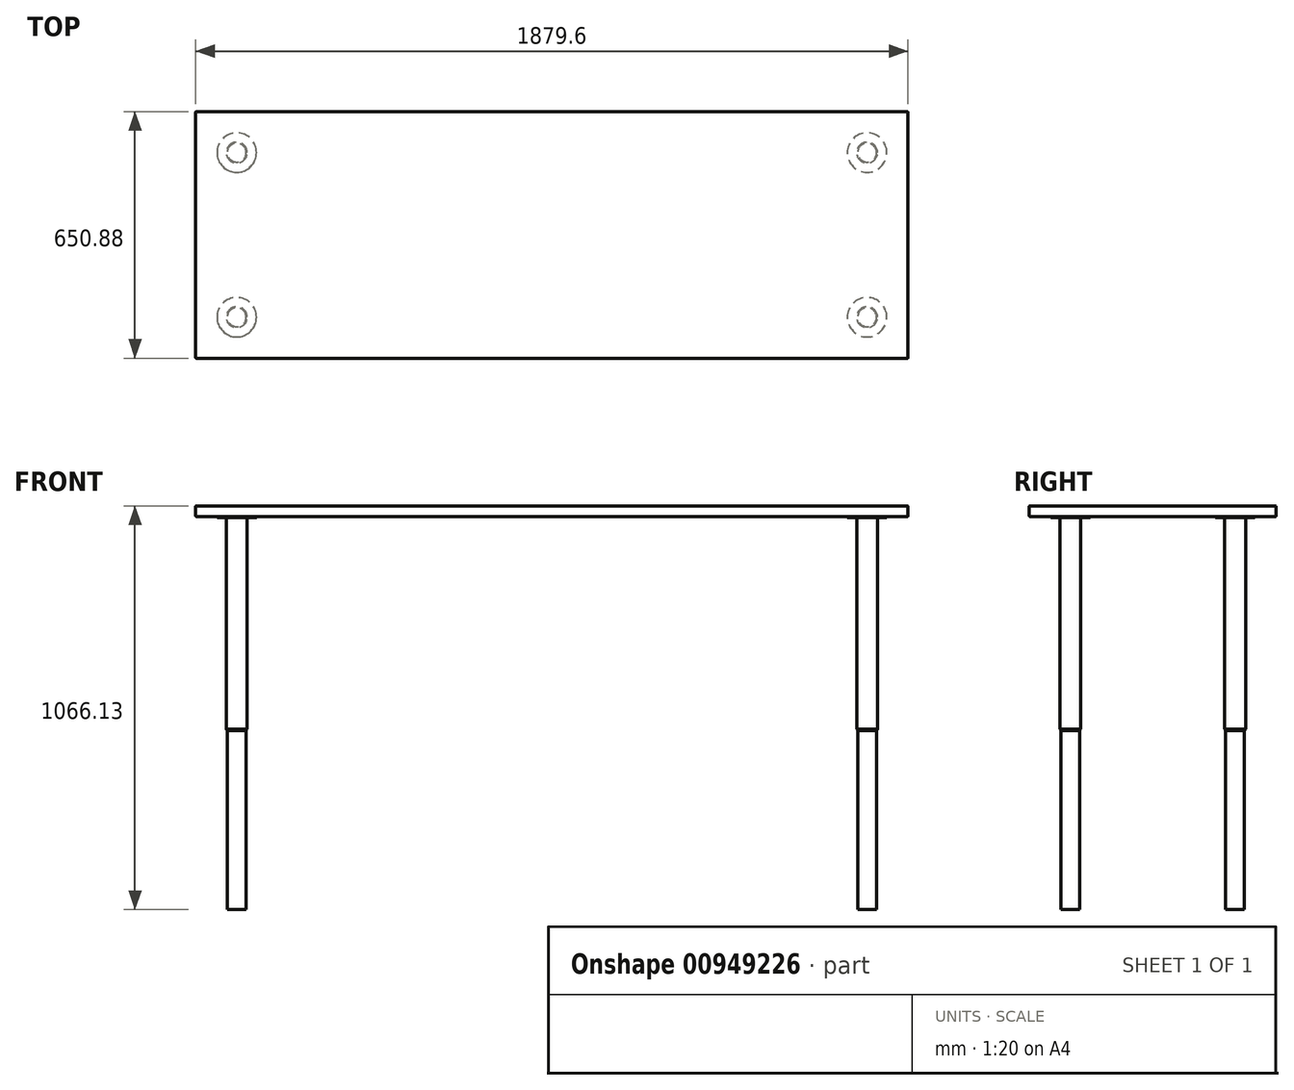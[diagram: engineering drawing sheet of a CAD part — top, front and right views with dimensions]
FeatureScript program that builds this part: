
annotation { "Feature Type Name" : "Feature", "Feature Type Description" : "" }
export const myFeature = defineFeature(function(context is Context, id is Id, definition is map)
    precondition{}
    {
        {
            var Q0;
            Q0=qCreatedBy(makeId("Top.planeOp"),FACE);
            var sketch = newSketch(context, id + "F0", { "sketchPlane" : qUnion([Q0])});
            skLineSegment(sketch, "E0.bottom", {"start": v(-939.8, 325.44) * mm, "end": v(939.8, 325.44) * mm});
            skLineSegment(sketch, "E0.top", {"start": v(-939.8, -325.44) * mm, "end": v(939.8, -325.44) * mm});
            skLineSegment(sketch, "E0.left", {"start": v(-939.8, 325.44) * mm, "end": v(-939.8, -325.44) * mm});
            skLineSegment(sketch, "E0.right", {"start": v(939.8, 325.44) * mm, "end": v(939.8, -325.44) * mm});
            skPoint(sketch, "E0.middle", {"position": v(0, 0) * mm});
            skSolve(sketch);
        }
        {
            var Q0;
            Q0 = qSketchRegion(id + "F0", true);
            extrude(context, id + "F1", {"entities" : qUnion([Q0]), "depth" : 28.2 * mm, "offsetDistance" : 25 * mm});
        }
        {
            var Q0;
            Q0=makeQuery(id+"F1.opExtrude","CAP_EDGE",EDGE,{"disambiguationData":[OSD([sQuery(id+"F0.wireOp",EDGE,"E0.top")])],"isStart":false});
            var Q1;
            Q1=makeQuery(id+"F1.opExtrude","CAP_EDGE",EDGE,{"disambiguationData":[OSD([sQuery(id+"F0.wireOp",EDGE,"E0.top")])],"isStart":true});
            var Q2;
            Q2=makeQuery(id+"F1.opExtrude","CAP_EDGE",EDGE,{"disambiguationData":[OSD([sQuery(id+"F0.wireOp",EDGE,"E0.left")])],"isStart":false});
            var Q3;
            Q3=makeQuery(id+"F1.opExtrude","CAP_EDGE",EDGE,{"disambiguationData":[OSD([sQuery(id+"F0.wireOp",EDGE,"E0.bottom")])],"isStart":false});
            var Q4;
            Q4=makeQuery(id+"F1.opExtrude","CAP_EDGE",EDGE,{"disambiguationData":[OSD([sQuery(id+"F0.wireOp",EDGE,"E0.right")])],"isStart":false});
            var Q5;
            Q5=makeQuery(id+"F1.opExtrude","CAP_EDGE",EDGE,{"disambiguationData":[OSD([sQuery(id+"F0.wireOp",EDGE,"E0.right")])],"isStart":true});
            var Q6;
            Q6=makeQuery(id+"F1.opExtrude","CAP_EDGE",EDGE,{"disambiguationData":[OSD([sQuery(id+"F0.wireOp",EDGE,"E0.bottom")])],"isStart":true});
            var Q7;
            Q7=makeQuery(id+"F1.opExtrude","CAP_EDGE",EDGE,{"disambiguationData":[OSD([sQuery(id+"F0.wireOp",EDGE,"E0.left")])],"isStart":true});
            var Q8;
            Q8=makeQuery(id+"F1.opExtrude","SWEPT_EDGE",EDGE,{"disambiguationData":[OSD([sQuery(id+"F0.wireOp",EDGE,"E0.top"),sQuery(id+"F0.wireOp",EDGE,"E0.left")])]});
            var Q9;
            Q9=makeQuery(id+"F1.opExtrude","SWEPT_EDGE",EDGE,{"disambiguationData":[OSD([sQuery(id+"F0.wireOp",EDGE,"E0.bottom"),sQuery(id+"F0.wireOp",EDGE,"E0.left")])]});
            var Q10;
            Q10=makeQuery(id+"F1.opExtrude","SWEPT_EDGE",EDGE,{"disambiguationData":[OSD([sQuery(id+"F0.wireOp",EDGE,"E0.bottom"),sQuery(id+"F0.wireOp",EDGE,"E0.right")])]});
            var Q11;
            Q11=makeQuery(id+"F1.opExtrude","SWEPT_EDGE",EDGE,{"disambiguationData":[OSD([sQuery(id+"F0.wireOp",EDGE,"E0.top"),sQuery(id+"F0.wireOp",EDGE,"E0.right")])]});
            fillet(context, id + "F2", {"entities" : qUnion([Q0, Q1, Q2, Q3, Q4, Q5, Q6, Q7, Q8, Q9, Q10, Q11]), "radius" : 1 * mm, "tangentPropagation" : true, "allowEdgeOverflow" : false});
        }
        {
            var Q0;
            Q0=makeQuery(id+"F1.opExtrude","CAP_FACE",FACE,{"disambiguationData":[OSD([sQuery(id+"F0.wireOp",EDGE,"E0.bottom"),sQuery(id+"F0.wireOp",EDGE,"E0.top"),sQuery(id+"F0.wireOp",EDGE,"E0.left"),sQuery(id+"F0.wireOp",EDGE,"E0.right")])],"isStart":true});
            var sketch = newSketch(context, id + "F3", { "sketchPlane" : qUnion([Q0])});
            skCircle(sketch, "E1", {"center": v(-831.7, 217.34) * mm, "radius": 52.1 * mm});
            skLineSegment(sketch, "E2", {"start": v(-831.7, 217.34) * mm, "end": v(-831.7, 324.44) * mm, "construction": true});
            skLineSegment(sketch, "E3", {"start": v(-831.7, 217.34) * mm, "end": v(-938.8, 217.34) * mm, "construction": true});
            skSolve(sketch);
        }
        {
            var Q0;
            Q0 = qSketchRegion(id + "F3", true);
            extrude(context, id + "F4", {"entities" : qUnion([Q0]), "depth" : 2.62 * mm, "offsetDistance" : 25 * mm});
        }
        {
            var Q0;
            Q0=makeQuery(id+"F4.opExtrude","CAP_FACE",FACE,{"disambiguationData":[OSD([sQuery(id+"F3.wireOp",EDGE,"E1")])],"isStart":false});
            var sketch = newSketch(context, id + "F5", { "sketchPlane" : qUnion([Q0])});
            skCircle(sketch, "E4", {"center": v(-831.7, 217.34) * mm, "radius": 27.6 * mm});
            skSolve(sketch);
        }
        {
            var Q0;
            Q0 = qSketchRegion(id + "F5", true);
            extrude(context, id + "F6", {"entities" : qUnion([Q0]), "operationType" : NewBodyOperationType.ADD, "depth" : (22 * 25.4) * mm, "offsetDistance" : 25 * mm});
        }
        {
            var Q0;
            Q0=makeQuery(id+"F6.opExtrude","CAP_FACE",FACE,{"disambiguationData":[OSD([sQuery(id+"F5.wireOp",EDGE,"E4")])],"isStart":false});
            cPlane(context, id + "F7", {"entities" : qUnion([Q0]), "cplaneType" : CPlaneType.OFFSET, "offset" : 3.43 * mm, "width" : 150 * mm, "height" : 150 * mm});
        }
        {
            var Q0;
            Q0=qCreatedBy(id+"F7.planeOp",FACE);
            var sketch = newSketch(context, id + "F8", { "sketchPlane" : qUnion([Q0])});
            skCircle(sketch, "E5.0", {"center": v(-831.7, 217.34) * mm, "radius": 27.6 * mm, "construction": true});
            skCircle(sketch, "E6", {"center": v(-831.7, 217.34) * mm, "radius": 24.95 * mm});
            skSolve(sketch);
        }
        {
            var Q0;
            Q0 = qSketchRegion(id + "F8", true);
            var Q1;
            Q1 = qConstructionFilter(qBodyType(qCreatedBy(id + "F8" ,EDGE), BodyType.WIRE), ConstructionObject.NO);
            extrude(context, id + "F9", {"entities" : qUnion([Q0]), "surfaceEntities" : qUnion([Q1]), "depth" : ((18 + 5 / 8) * 25.4) * mm, "offsetDistance" : 25 * mm});
        }
        {
            var Q0;
            Q0=makeQuery(id+"F6.opExtrude","CAP_FACE",FACE,{"disambiguationData":[OSD([sQuery(id+"F5.wireOp",EDGE,"E4")])],"isStart":false});
            var Q1;
            Q1=makeQuery(id+"F9.opExtrude","CAP_FACE",FACE,{"disambiguationData":[OSD([sQuery(id+"F8.wireOp",EDGE,"E6")])],"isStart":true});
            loft(context, id + "F10", {"operationType" : NewBodyOperationType.ADD, "sheetProfilesArray" : [{ "sheetProfileEntities" : qUnion([Q0]) }, { "sheetProfileEntities" : qUnion([Q1]) }]});
        }
        {
            var Q0;
            Q0=makeQuery(id+"F4.opExtrude","SWEPT_BODY",BODY,{"disambiguationData":[OSD([sQuery(id+"F3.wireOp",EDGE,"E1")])]});
            var Q1;
            Q1=qCreatedBy(makeId("Front.planeOp"),FACE);
            mirror(context, id + "F11", {"entities" : qUnion([Q0]), "mirrorPlane" : qUnion([Q1])});
        }
        {
            var Q0;
            Q0=makeQuery(id+"F4.opExtrude","SWEPT_BODY",BODY,{"disambiguationData":[OSD([sQuery(id+"F3.wireOp",EDGE,"E1")])]});
            var Q1;
            Q1=makeQuery(id+"F11.opPattern","COPY",BODY,{"derivedFrom":makeQuery(id+"F4.opExtrude","SWEPT_BODY",BODY,{"disambiguationData":[OSD([sQuery(id+"F3.wireOp",EDGE,"E1")])]}),"instanceName":"1"});
            var Q2;
            Q2=qCreatedBy(makeId("Right.planeOp"),FACE);
            mirror(context, id + "F12", {"operationType" : NewBodyOperationType.ADD, "entities" : qUnion([Q0, Q1]), "mirrorPlane" : qUnion([Q2])});
        }
    });
